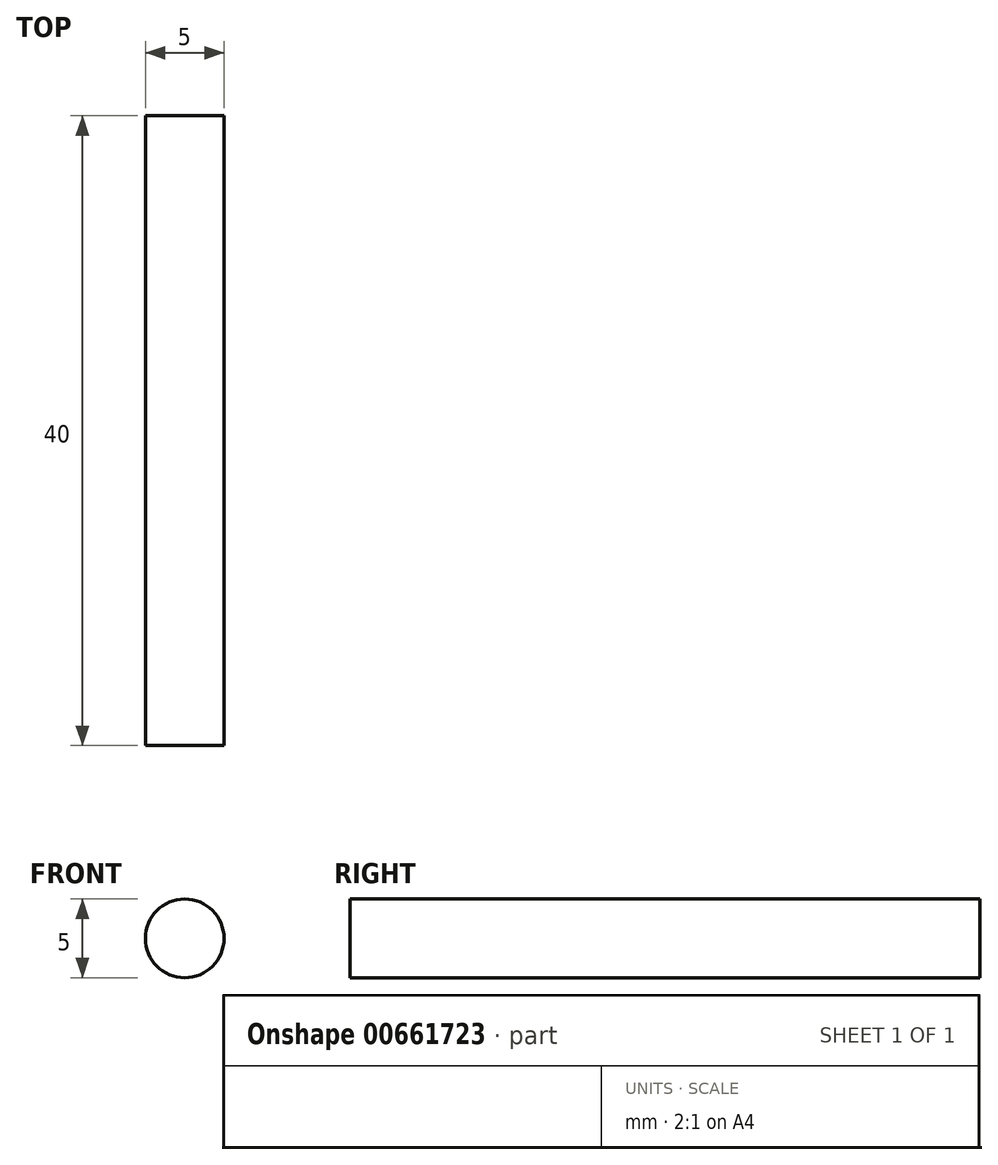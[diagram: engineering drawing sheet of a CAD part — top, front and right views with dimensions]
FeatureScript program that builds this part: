
annotation { "Feature Type Name" : "Feature", "Feature Type Description" : "" }
export const myFeature = defineFeature(function(context is Context, id is Id, definition is map)
    precondition{}
    {
        {
            var Q0;
            Q0=qCreatedBy(makeId("Front.planeOp"),FACE);
            var sketch = newSketch(context, id + "F0", { "sketchPlane" : qUnion([Q0])});
            skCircle(sketch, "E0", {"center": v(0, 0) * mm, "radius": 2.5 * mm});
            skSolve(sketch);
        }
        {
            var Q0;
            Q0 = qSketchRegion(id + "F0", true);
            extrude(context, id + "F1", {"entities" : qUnion([Q0]), "depth" : 40 * mm, "offsetDistance" : 25 * mm});
        }
    });
